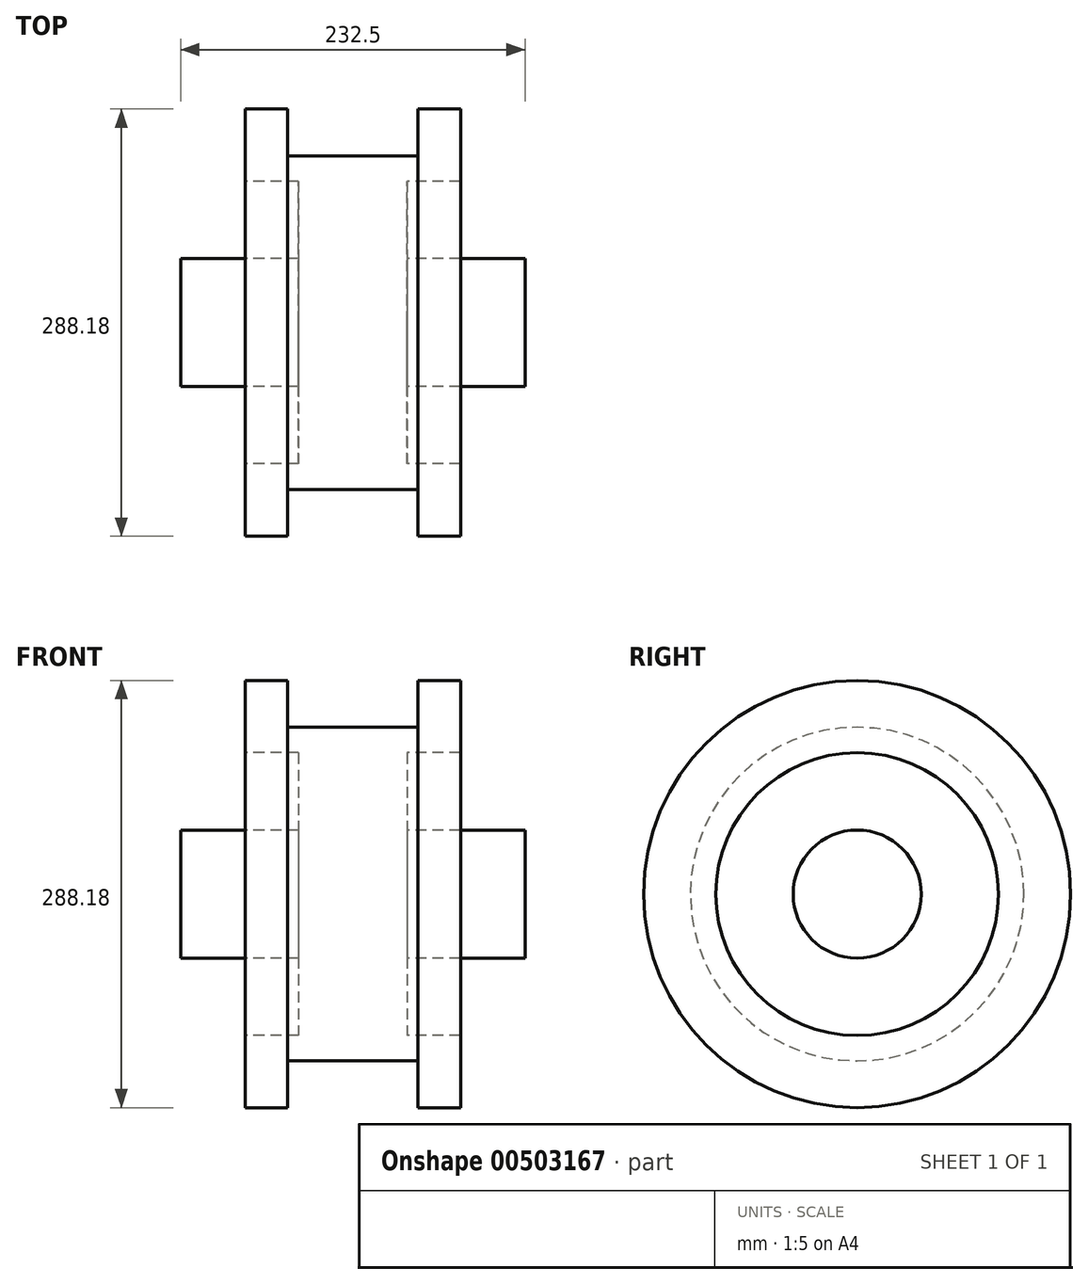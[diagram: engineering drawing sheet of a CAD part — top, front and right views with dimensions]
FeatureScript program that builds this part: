
annotation { "Feature Type Name" : "Feature", "Feature Type Description" : "" }
export const myFeature = defineFeature(function(context is Context, id is Id, definition is map)
    precondition{}
    {
        {
            var Q0;
            Q0=qCreatedBy(makeId("Front.planeOp"),FACE);
            var sketch = newSketch(context, id + "F0", { "sketchPlane" : qUnion([Q0])});
            skLineSegment(sketch, "E0", {"start": v(-151.39, 0) * mm, "end": v(152.74, 0) * mm, "construction": true});
            skLineSegment(sketch, "E1", {"start": v(0, 0) * mm, "end": v(0, 134.53) * mm, "construction": true});
            skLineSegment(sketch, "E2", {"start": v(-72.69, 144.09) * mm, "end": v(-72.69, 95.37) * mm});
            skLineSegment(sketch, "E3", {"start": v(-72.69, 95.37) * mm, "end": v(-36.58, 95.37) * mm});
            skLineSegment(sketch, "E4", {"start": v(-36.58, 95.37) * mm, "end": v(-36.58, 43.2) * mm});
            skLineSegment(sketch, "E5", {"start": v(-36.58, 43.2) * mm, "end": v(-116.25, 43.2) * mm});
            skLineSegment(sketch, "E6", {"start": v(-116.25, 43.2) * mm, "end": v(-116.25, 0) * mm});
            skLineSegment(sketch, "E7", {"start": v(-116.25, 0) * mm, "end": v(0, 0) * mm});
            skLineSegment(sketch, "E8", {"start": v(0, 0) * mm, "end": v(-116.25, 0) * mm});
            skLineSegment(sketch, "E9", {"start": v(-72.69, 144.09) * mm, "end": v(-44.03, 144.09) * mm});
            skLineSegment(sketch, "E10", {"start": v(-44.03, 144.09) * mm, "end": v(-44.03, 112.56) * mm});
            skLineSegment(sketch, "E11", {"start": v(-44.03, 112.56) * mm, "end": v(0, 112.56) * mm});
            skLineSegment(sketch, "E12.MirrorCS", {"start": v(72.69, 144.09) * mm, "end": v(72.69, 95.37) * mm});
            skLineSegment(sketch, "E13.MirrorCS", {"start": v(72.69, 95.37) * mm, "end": v(36.58, 95.37) * mm});
            skLineSegment(sketch, "E14.MirrorCS", {"start": v(72.69, 144.09) * mm, "end": v(44.03, 144.09) * mm});
            skLineSegment(sketch, "E15.MirrorCS", {"start": v(44.03, 144.09) * mm, "end": v(44.03, 112.56) * mm});
            skLineSegment(sketch, "E16.MirrorCS", {"start": v(36.58, 43.2) * mm, "end": v(116.25, 43.2) * mm});
            skLineSegment(sketch, "E17.MirrorCS", {"start": v(36.58, 95.37) * mm, "end": v(36.58, 43.2) * mm});
            skLineSegment(sketch, "E18.MirrorCS", {"start": v(116.25, 43.2) * mm, "end": v(116.25, 0) * mm});
            skLineSegment(sketch, "E19", {"start": v(44.03, 112.56) * mm, "end": v(0, 112.56) * mm});
            skLineSegment(sketch, "E20", {"start": v(116.25, 0) * mm, "end": v(-116.25, 0) * mm});
            skSolve(sketch);
        }
        {
            var Q0;
            Q0=makeQuery(id+"F0.imprint","IMPRINT",FACE,{"disambiguationData":[TD([[makeQuery(id+"F0.imprint","IMPRINT",EDGE,{"derivedFrom":sQuery(id+"F0.wireOp",EDGE,"E2")}),1.0]])]});
            var Q1;
            Q1=sQuery(id+"F0.wireOp",EDGE,"E0");
            revolve(context, id + "F1", {"entities" : qUnion([Q0]), "axis" : qUnion([Q1]), "revolveType" : RevolveType.FULL});
        }
    });
